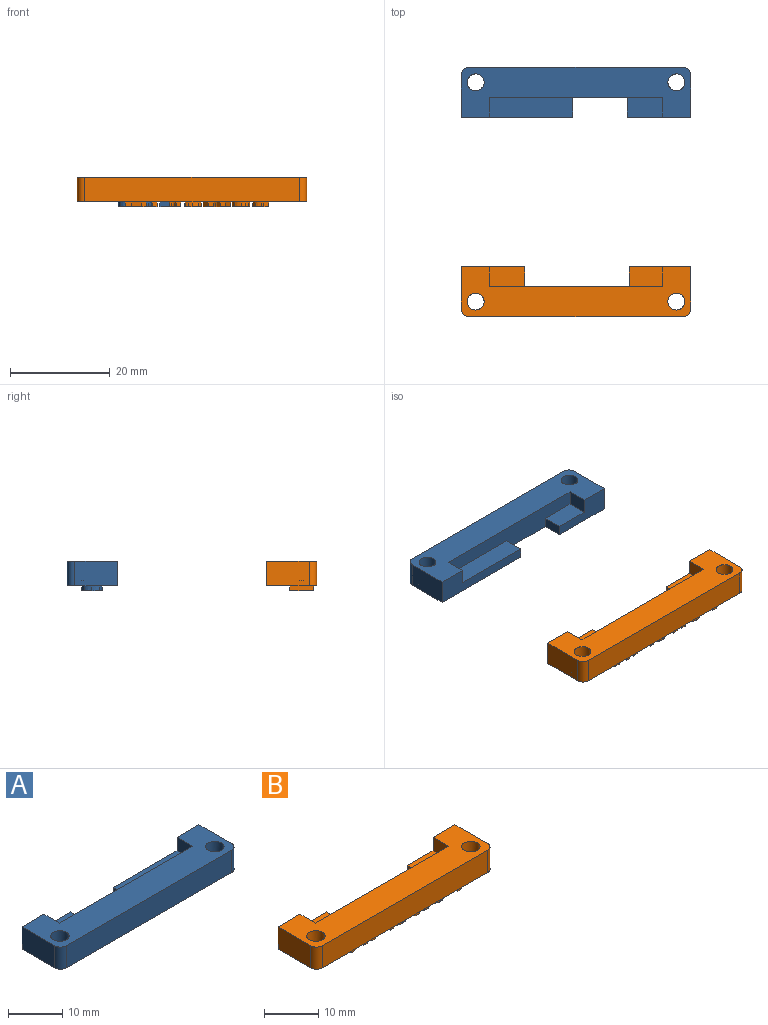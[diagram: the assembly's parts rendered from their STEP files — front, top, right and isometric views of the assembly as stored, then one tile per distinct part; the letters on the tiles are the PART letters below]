
ASSEMBLY  parts=2 mates=1
PART A: 63 faces, bbox 46x10x6 mm
  f0: plane 46x10mm, normal (0,0,-1), area 344.5mm2, adj f2,f4,f5,f6,f7,f10,f12,f13
  f1: plane 16.6x4mm, normal (0,0,1), area 66.4mm2, adj f6,f9,f10,f13
  f2: plane 12.7x5mm, normal (0,1,0), area 42.5mm2, adj f0,f3,f7,f8,f11,f12
  f3: plane 7x4mm, normal (0,0,1), area 28mm2, adj f2,f8,f10,f12
  f4: plane 43x5mm, normal (0,-1,0), area 215mm2, adj f0,f11,f20,f21
  f5: plane 8.5x5mm, normal (1,0,0), area 42.5mm2, adj f0,f6,f11,f20
  f6: plane 22.3x5mm, normal (0,1,0), area 61.7mm2, adj f0,f1,f5,f9,f11,f13
  f7: plane 8.5x5mm, normal (-1,0,0), area 42.5mm2, adj f0,f2,f11,f21
  f8: plane 4x3mm, normal (1,0,0), area 12mm2, adj f2,f3,f10,f11
  f9: plane 4x3mm, normal (-1,0,0), area 12mm2, adj f1,f6,f10,f11
  f10: plane 34.6x5mm, normal (0,1,0), area 125.8mm2, adj f0,f1,f3,f8,f9,f11,f12,f13
  f11: plane 46x10mm, normal (0,0,1), area 302.5mm2, adj f2,f4,f5,f6,f7,f8,f9,f10
  f12: plane 4x2mm, normal (1,0,0), area 8mm2, adj f0,f2,f3,f10
  f13: plane 4x2mm, normal (-1,0,0), area 8mm2, adj f0,f1,f6,f10
  f14: cylinder r=1.7mm len=4mm, axis (0,0,-1), area 42.7mm2, adj f11,f15
  f15: plane 5.4x5.4mm, normal (0,0,-1), area 13.8mm2, adj f14,f16
  f16: cylinder r=2.7mm len=5.4mm, axis (0,0,-1), area 17mm2, adj f0,f15
  f17: cylinder r=1.7mm len=4mm, axis (0,0,-1), area 42.7mm2, adj f11,f18
  f18: plane 5.4x5.4mm, normal (0,0,-1), area 13.8mm2, adj f17,f19
  f19: cylinder r=2.7mm len=5.4mm, axis (0,0,-1), area 17mm2, adj f0,f18
  f20: cylinder r=1.5mm len=5mm, axis (0,0,1), area 11.8mm2, adj f0,f4,f5,f11
  f21: cylinder r=1.5mm len=5mm, axis (0,0,-1), area 11.8mm2, adj f0,f4,f7,f11
  f22: extruded ~1x1mm, area 1mm2, adj f23,f35,f36,f37
  f23: extruded ~1x1mm, area 1.1mm2, adj f22,f24,f36,f37
  f24: extruded ~1x0.76mm, area 0.9mm2, adj f23,f25,f36,f37
  f25: extruded ~1.34x1mm, area 1.9mm2, adj f24,f26,f36,f37
  f26: extruded ~1.34x1.01mm, area 1.9mm2, adj f25,f35,f36,f37
  f27: extruded ~1.51x1mm, area 1.6mm2, adj f0,f28,f34,f36
  f28: extruded ~1.51x1mm, area 1.6mm2, adj f0,f27,f29,f36
  f29: extruded ~1.4x1mm, area 1.5mm2, adj f0,f28,f30,f36
  f30: extruded ~1.4x1mm, area 1.5mm2, adj f0,f29,f31,f36
  f31: extruded ~1.51x1mm, area 1.6mm2, adj f0,f30,f32,f36
  f32: extruded ~1.52x1mm, area 1.6mm2, adj f0,f31,f33,f36
  f33: extruded ~1.4x1mm, area 1.5mm2, adj f0,f32,f34,f36
  f34: extruded ~1.4x1mm, area 1.5mm2, adj f0,f27,f33,f36
  f35: extruded ~1x0.75mm, area 0.9mm2, adj f22,f26,f36,f37
  f36: plane 4.08x3.78mm, normal (0,0,-1), area 8.2mm2, adj f22,f23,f24,f25,f26,f27,f28,f29
  f37: plane 2.68x2.01mm, normal (0,0,-1), area 4.5mm2, adj f22,f23,f24,f25,f26,f35
  f38: plane 2.57x1mm, normal (-1,0,0), area 2.6mm2, adj f0,f39,f52,f53
  f39: plane 1x0.84mm, normal (0,1,0), area 0.8mm2, adj f0,f38,f40,f53
  f40: plane 2.42x1mm, normal (1,0,0), area 2.4mm2, adj f0,f39,f41,f53
  f41: extruded ~1x0.68mm, area 0.7mm2, adj f0,f40,f42,f53
  f42: extruded ~1x0.6mm, area 0.7mm2, adj f0,f41,f43,f53
  f43: extruded ~1x0.61mm, area 0.7mm2, adj f0,f42,f44,f53
  f44: extruded ~1x0.67mm, area 0.7mm2, adj f0,f43,f45,f53
  f45: plane 2.43x1mm, normal (-1,0,0), area 2.4mm2, adj f0,f44,f46,f53
  f46: plane 1x0.84mm, normal (0,1,0), area 0.8mm2, adj f0,f45,f47,f53
  f47: plane 2.56x1mm, normal (1,0,0), area 2.6mm2, adj f0,f46,f48,f53
  f48: extruded ~1.07x1mm, area 1.2mm2, adj f0,f47,f49,f53
  f49: extruded ~1.19x1mm, area 1.3mm2, adj f0,f48,f50,f53
  f50: extruded ~1x0.88mm, area 0.9mm2, adj f0,f49,f51,f53
  f51: extruded ~1x0.57mm, area 0.8mm2, adj f0,f50,f52,f53
  f52: extruded ~1x0.77mm, area 0.8mm2, adj f0,f38,f51,f53
  f53: plane 4.02x3.26mm, normal (0,0,-1), area 7.2mm2, adj f38,f39,f40,f41,f42,f43,f44,f45
  f54: plane 1x0.84mm, normal (0,-1,0), area 0.8mm2, adj f0,f55,f61,f62
  f55: plane 3.27x1mm, normal (-1,0,0), area 3.3mm2, adj f0,f54,f56,f62
  f56: plane 1.08x1mm, normal (0,-1,0), area 1.1mm2, adj f0,f55,f57,f62
  f57: plane 1x0.7mm, normal (-1,0,0), area 0.7mm2, adj f0,f56,f58,f62
  f58: plane 2.99x1mm, normal (0,1,0), area 3mm2, adj f0,f57,f59,f62
  f59: plane 1x0.7mm, normal (1,0,0), area 0.7mm2, adj f0,f58,f60,f62
  f60: plane 1.08x1mm, normal (0,-1,0), area 1.1mm2, adj f0,f59,f61,f62
  f61: plane 3.27x1mm, normal (1,0,0), area 3.3mm2, adj f0,f54,f60,f62
  f62: plane 3.97x2.99mm, normal (0,0,-1), area 4.8mm2, adj f54,f55,f56,f57,f58,f59,f60,f61
PART B: 143 faces, bbox 46x10x6 mm
  f0: plane 6.64x4mm, normal (0,0,1), area 26.5mm2, adj f5,f9,f10,f13
  f1: plane 12.7x5mm, normal (0,1,0), area 42.5mm2, adj f2,f6,f7,f8,f11,f12
  f2: plane 7x4mm, normal (0,0,1), area 28mm2, adj f1,f8,f10,f12
  f3: plane 43x5mm, normal (0,-1,0), area 215mm2, adj f7,f11,f20,f21
  f4: plane 8.5x5mm, normal (1,0,0), area 42.5mm2, adj f5,f7,f11,f20
  f5: plane 12.34x5mm, normal (0,1,0), area 41.8mm2, adj f0,f4,f7,f9,f11,f13
  f6: plane 8.5x5mm, normal (-1,0,0), area 42.5mm2, adj f1,f7,f11,f21
  f7: plane 46x10mm, normal (0,0,-1), area 266.8mm2, adj f1,f3,f4,f5,f6,f10,f12,f13
  f8: plane 4x3mm, normal (1,0,0), area 12mm2, adj f1,f2,f10,f11
  f9: plane 4x3mm, normal (-1,0,0), area 12mm2, adj f0,f5,f10,f11
  f10: plane 34.6x5mm, normal (0,1,0), area 145.7mm2, adj f0,f2,f7,f8,f9,f11,f12,f13
  f11: plane 46x10mm, normal (0,0,1), area 302.5mm2, adj f1,f3,f4,f5,f6,f8,f9,f10
  f12: plane 4x2mm, normal (1,0,0), area 8mm2, adj f1,f2,f7,f10
  f13: plane 4x2mm, normal (-1,0,0), area 8mm2, adj f0,f5,f7,f10
  f14: cylinder r=1.7mm len=4mm, axis (0,0,-1), area 42.7mm2, adj f11,f15
  f15: plane 5.4x5.4mm, normal (0,0,-1), area 13.8mm2, adj f14,f16
  f16: cylinder r=2.7mm len=5.4mm, axis (0,0,-1), area 17mm2, adj f7,f15
  f17: cylinder r=1.7mm len=4mm, axis (0,0,-1), area 42.7mm2, adj f11,f18
  f18: plane 5.4x5.4mm, normal (0,0,-1), area 13.8mm2, adj f17,f19
  f19: cylinder r=2.7mm len=5.4mm, axis (0,0,-1), area 17mm2, adj f7,f18
  f20: cylinder r=1.5mm len=5mm, axis (0,0,1), area 11.8mm2, adj f3,f4,f7,f11
  f21: cylinder r=1.5mm len=5mm, axis (0,0,-1), area 11.8mm2, adj f3,f6,f7,f11
  f22: extruded ~1.16x1mm, area 1.3mm2, adj f7,f23,f37,f38
  f23: extruded ~1.1x1mm, area 1.2mm2, adj f7,f22,f24,f38
  f24: extruded ~1.3x1mm, area 1.4mm2, adj f7,f23,f25,f38
  f25: plane 1.5x1mm, normal (0,1,0), area 1.5mm2, adj f7,f24,f26,f38
  f26: plane 4.7x1mm, normal (1,0,0), area 4.7mm2, adj f7,f25,f27,f38
  f27: plane 1x1mm, normal (0,-1,0), area 1mm2, adj f7,f26,f28,f38
  f28: plane 1.67x1mm, normal (-1,0,0), area 1.7mm2, adj f7,f27,f29,f38
  f29: plane 1x0.43mm, normal (0,-1,0), area 0.4mm2, adj f7,f28,f37,f38
  f30: plane 1x0.33mm, normal (0,1,0), area 0.3mm2, adj f31,f36,f38,f39
  f31: plane 1.39x1mm, normal (-1,0,0), area 1.4mm2, adj f30,f32,f38,f39
  f32: plane 1x0.45mm, normal (0,-1,0), area 0.5mm2, adj f31,f33,f38,f39
  f33: extruded ~1x0.6mm, area 0.6mm2, adj f32,f34,f38,f39
  f34: extruded ~1x0.52mm, area 0.6mm2, adj f33,f35,f38,f39
  f35: extruded ~1x0.53mm, area 0.6mm2, adj f34,f36,f38,f39
  f36: extruded ~1x0.69mm, area 0.7mm2, adj f30,f35,f38,f39
  f37: extruded ~1.35x1mm, area 1.4mm2, adj f7,f22,f29,f38
  f38: plane 4.7x3.25mm, normal (0,0,-1), area 9mm2, adj f22,f23,f24,f25,f26,f27,f28,f29
  f39: plane 1.39x1.24mm, normal (0,0,-1), area 1.5mm2, adj f30,f31,f32,f33,f34,f35,f36
  f40: extruded ~1.37x1mm, area 1.5mm2, adj f7,f41,f57,f58
  f41: extruded ~1x0.99mm, area 1mm2, adj f7,f40,f42,f58
  f42: extruded ~1x0.65mm, area 0.9mm2, adj f7,f41,f43,f58
  f43: extruded ~1x0.91mm, area 1mm2, adj f7,f42,f44,f58
  f44: extruded ~1.29x1mm, area 1.4mm2, adj f7,f43,f45,f58
  f45: extruded ~1.37x1mm, area 1.5mm2, adj f7,f44,f46,f58
  f46: extruded ~1x0.99mm, area 1mm2, adj f7,f45,f47,f58
  f47: extruded ~1x0.65mm, area 0.9mm2, adj f7,f46,f48,f58
  f48: extruded ~1x0.91mm, area 1mm2, adj f7,f47,f57,f58
  f49: extruded ~1x0.81mm, area 0.8mm2, adj f50,f56,f58,f59
  f50: extruded ~1x0.8mm, area 0.8mm2, adj f49,f51,f58,f59
  f51: extruded ~1x0.57mm, area 0.7mm2, adj f50,f52,f58,f59
  f52: extruded ~1x0.57mm, area 0.7mm2, adj f51,f53,f58,f59
  f53: extruded ~1x0.8mm, area 0.8mm2, adj f52,f54,f58,f59
  f54: extruded ~1x0.81mm, area 0.8mm2, adj f53,f55,f58,f59
  f55: extruded ~1x0.56mm, area 0.7mm2, adj f54,f56,f58,f59
  f56: extruded ~1x0.57mm, area 0.7mm2, adj f49,f55,f58,f59
  f57: extruded ~1.29x1mm, area 1.4mm2, adj f7,f40,f48,f58
  f58: plane 3.73x3.48mm, normal (0,0,-1), area 7.9mm2, adj f40,f41,f42,f43,f44,f45,f46,f47
  f59: plane 2.15x1.48mm, normal (0,0,-1), area 2.7mm2, adj f49,f50,f51,f52,f53,f54,f55,f56
  f60: plane 1.26x1mm, normal (0.98,-0.21,0), area 1.3mm2, adj f7,f61,f85,f86
  f61: plane 1.07x1mm, normal (0,-1,0), area 1.1mm2, adj f7,f60,f62,f86
  f62: plane 3.59x1.04mm, normal (-0.96,-0.28,0), area 3.7mm2, adj f7,f61,f63,f86
  f63: plane 1x0.96mm, normal (0,1,0), area 1mm2, adj f7,f62,f64,f86
  f64: plane 1.59x1mm, normal (0.97,0.26,0), area 1.6mm2, adj f7,f63,f65,f86
  f65: extruded ~1x0.55mm, area 0.6mm2, adj f7,f64,f66,f86
  f66: extruded ~1x0.63mm, area 0.6mm2, adj f7,f65,f67,f86
  f67: plane 1x0.02mm, normal (0,1,0), area 0mm2, adj f7,f66,f68,f86
  f68: extruded ~1x0.24mm, area 0.2mm2, adj f7,f67,f69,f86
  f69: extruded ~1x0.31mm, area 0.3mm2, adj f7,f68,f70,f86
  f70: extruded ~1x0.29mm, area 0.3mm2, adj f7,f69,f71,f86
  f71: extruded ~1x0.21mm, area 0.2mm2, adj f7,f70,f72,f86
  f72: plane 1.72x1mm, normal (-0.97,0.24,0), area 1.8mm2, adj f7,f71,f73,f86
  f73: plane 1.08x1mm, normal (0,1,0), area 1.1mm2, adj f7,f72,f74,f86
  f74: plane 1.72x1mm, normal (0.97,0.25,0), area 1.8mm2, adj f7,f73,f75,f86
  f75: plane 1x0.27mm, normal (0.98,0.18,0), area 0.3mm2, adj f7,f74,f76,f86
  f76: extruded ~1x0.77mm, area 0.8mm2, adj f7,f75,f77,f86
  f77: plane 1x0.02mm, normal (0,1,0), area 0mm2, adj f7,f76,f78,f86
  f78: extruded ~1.18x1mm, area 1.2mm2, adj f7,f77,f79,f86
  f79: plane 1.59x1mm, normal (-0.97,0.25,0), area 1.6mm2, adj f7,f78,f80,f86
  f80: plane 1x0.98mm, normal (0,1,0), area 1mm2, adj f7,f79,f81,f86
  f81: plane 3.59x1.02mm, normal (0.96,-0.27,0), area 3.7mm2, adj f7,f80,f82,f86
  f82: plane 1.05x1mm, normal (0,-1,0), area 1.1mm2, adj f7,f81,f83,f86
  f83: plane 2.84x1mm, normal (-0.97,-0.22,0), area 2.9mm2, adj f7,f82,f84,f86
  f84: plane 1x0.02mm, normal (0,-1,0), area 0mm2, adj f7,f83,f85,f86
  f85: plane 1.59x1mm, normal (0.97,-0.23,0), area 1.6mm2, adj f7,f60,f84,f86
  f86: plane 5.51x3.59mm, normal (0,0,-1), area 11mm2, adj f60,f61,f62,f63,f64,f65,f66,f67
  f87: extruded ~1.36x1mm, area 1.5mm2, adj f7,f88,f106,f107
  f88: extruded ~1x0.71mm, area 0.7mm2, adj f7,f87,f89,f107
  f89: extruded ~1x0.55mm, area 0.6mm2, adj f7,f88,f90,f107
  f90: plane 1x0.76mm, normal (-1,0,0), area 0.8mm2, adj f7,f89,f91,f107
  f91: extruded ~1x0.6mm, area 0.6mm2, adj f7,f90,f92,f107
  f92: extruded ~1x0.61mm, area 0.6mm2, adj f7,f91,f93,f107
  f93: extruded ~1x0.65mm, area 0.7mm2, adj f7,f92,f94,f107
  f94: extruded ~1x0.65mm, area 0.7mm2, adj f7,f93,f95,f107
  f95: plane 2.32x1mm, normal (0,-1,0), area 2.3mm2, adj f7,f94,f96,f107
  f96: plane 1x0.48mm, normal (-1,0,0), area 0.5mm2, adj f7,f95,f97,f107
  f97: extruded ~1.2x1mm, area 1.3mm2, adj f7,f96,f98,f107
  f98: extruded ~1.19x1mm, area 1.3mm2, adj f7,f97,f99,f107
  f99: extruded ~1.25x1mm, area 1.4mm2, adj f7,f98,f100,f107
  f100: extruded ~1.4x1mm, area 1.5mm2, adj f7,f99,f106,f107
  f101: extruded ~1x0.49mm, area 0.5mm2, adj f102,f105,f107,f108
  f102: extruded ~1x0.49mm, area 0.5mm2, adj f101,f103,f107,f108
  f103: extruded ~1x0.56mm, area 0.6mm2, adj f102,f104,f107,f108
  f104: plane 1.38x1mm, normal (0,1,0), area 1.4mm2, adj f103,f105,f107,f108
  f105: extruded ~1x0.56mm, area 0.6mm2, adj f101,f104,f107,f108
  f106: extruded ~1.36x1mm, area 1.5mm2, adj f7,f87,f100,f107
  f107: plane 3.73x3.31mm, normal (0,0,-1), area 7.8mm2, adj f87,f88,f89,f90,f91,f92,f93,f94
  f108: plane 1.38x0.76mm, normal (0,0,-1), area 0.8mm2, adj f101,f102,f103,f104,f105
  f109: extruded ~1x0.33mm, area 0.3mm2, adj f7,f110,f121,f122
  f110: extruded ~1x0.62mm, area 0.7mm2, adj f7,f109,f111,f122
  f111: extruded ~1x0.49mm, area 0.7mm2, adj f7,f110,f112,f122
  f112: plane 1x0.05mm, normal (0,1,0), area 0mm2, adj f7,f111,f113,f122
  f113: plane 1x0.6mm, normal (-0.97,0.23,0), area 0.6mm2, adj f7,f112,f114,f122
  f114: plane 1x0.74mm, normal (0,1,0), area 0.7mm2, adj f7,f113,f115,f122
  f115: plane 3.59x1mm, normal (1,0,0), area 3.6mm2, adj f7,f114,f116,f122
  f116: plane 1x0.98mm, normal (0,-1,0), area 1mm2, adj f7,f115,f117,f122
  f117: plane 1.83x1mm, normal (-1,0,0), area 1.8mm2, adj f7,f116,f118,f122
  f118: extruded ~1x0.68mm, area 0.7mm2, adj f7,f117,f119,f122
  f119: extruded ~1x0.73mm, area 0.8mm2, adj f7,f118,f120,f122
  f120: extruded ~1x0.29mm, area 0.3mm2, adj f7,f119,f121,f122
  f121: plane 1x0.92mm, normal (-1,-0.08,0), area 0.9mm2, adj f7,f109,f120,f122
  f122: plane 3.66x2.34mm, normal (0,0,-1), area 4.6mm2, adj f109,f110,f111,f112,f113,f114,f115,f116
  f123: plane 4.7x1mm, normal (1,0,0), area 4.7mm2, adj f7,f124,f126,f127
  f124: plane 1x1mm, normal (0,-1,0), area 1mm2, adj f7,f123,f125,f127
  f125: plane 4.7x1mm, normal (-1,0,0), area 4.7mm2, adj f7,f124,f126,f127
  f126: plane 1x1mm, normal (0,1,0), area 1mm2, adj f7,f123,f125,f127
  f127: plane 4.7x1mm, normal (0,0,-1), area 4.7mm2, adj f123,f124,f125,f126
  f128: plane 1.27x1mm, normal (0,-1,0), area 1.3mm2, adj f7,f129,f141,f142
  f129: plane 4.7x1mm, normal (-1,0,0), area 4.7mm2, adj f7,f128,f130,f142
  f130: plane 1x0.9mm, normal (0,1,0), area 0.9mm2, adj f7,f129,f131,f142
  f131: plane 2.22x1mm, normal (1,0,0), area 2.2mm2, adj f7,f130,f132,f142
  f132: extruded ~1.3x1mm, area 1.3mm2, adj f7,f131,f133,f142
  f133: plane 1x0.02mm, normal (0,1,0), area 0mm2, adj f7,f132,f134,f142
  f134: plane 3.52x2.04mm, normal (-0.87,0.5,0), area 4.1mm2, adj f7,f133,f135,f142
  f135: plane 1.26x1mm, normal (0,1,0), area 1.3mm2, adj f7,f134,f136,f142
  f136: plane 4.7x1mm, normal (1,0,0), area 4.7mm2, adj f7,f135,f137,f142
  f137: plane 1x0.89mm, normal (0,-1,0), area 0.9mm2, adj f7,f136,f138,f142
  f138: plane 2.21x1mm, normal (-1,0,0), area 2.2mm2, adj f7,f137,f139,f142
  f139: extruded ~1.34x1mm, area 1.3mm2, adj f7,f138,f140,f142
  f140: plane 1x0.03mm, normal (0,-1,0), area 0mm2, adj f7,f139,f141,f142
  f141: plane 3.55x2.04mm, normal (0.87,-0.5,0), area 4.1mm2, adj f7,f128,f140,f142
  f142: plane 4.7x4.17mm, normal (0,0,-1), area 12.5mm2, adj f128,f129,f130,f131,f132,f133,f134,f135
PLACE A rot(axis=(0,0,1),180deg) t=(28.31,6.86,10.57)mm fixed
PLACE B t=(28.31,-33.14,10.57)mm
MATE slider B.f5 <-> A.f2  axis (0,1,0) through (51.31,-28.14,15.57)mm
